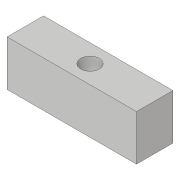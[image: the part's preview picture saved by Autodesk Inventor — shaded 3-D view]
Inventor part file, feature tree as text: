
AUTODESK INVENTOR PART (.ipt)
format: ipt  version: 2018.3 (Build 223284000, 284)  size: 93,184 bytes
history: native  units: in
note: dims shown in document units (in); Inventor stores cm internally (conversion verified against a paired STEP export)
features: extrude x2, sketch x2
ambient origin geometry x8: Origin, YZ Plane, XZ Plane, XY Plane, X Axis, Y Axis, Z Axis, Center Point
bodies: Solid1 (feature_tree)
feature tree (4):
  extrude  "Extrusion1"  Depth=1.25in
  extrude  "Extrusion2"  Depth=0.255in
  sketch  "Sketch1"  dims[d0=3.55in d1=1.25in]
  sketch  "Sketch2"  dims[d2=1.0in d3=0.0in d4=1.5in d5=1.5in d6=0.245in d7=0.245in d8=0.255in d10=0.275in d11=0.275in d12=0.51in d13=3.0in d14=0.0in]
